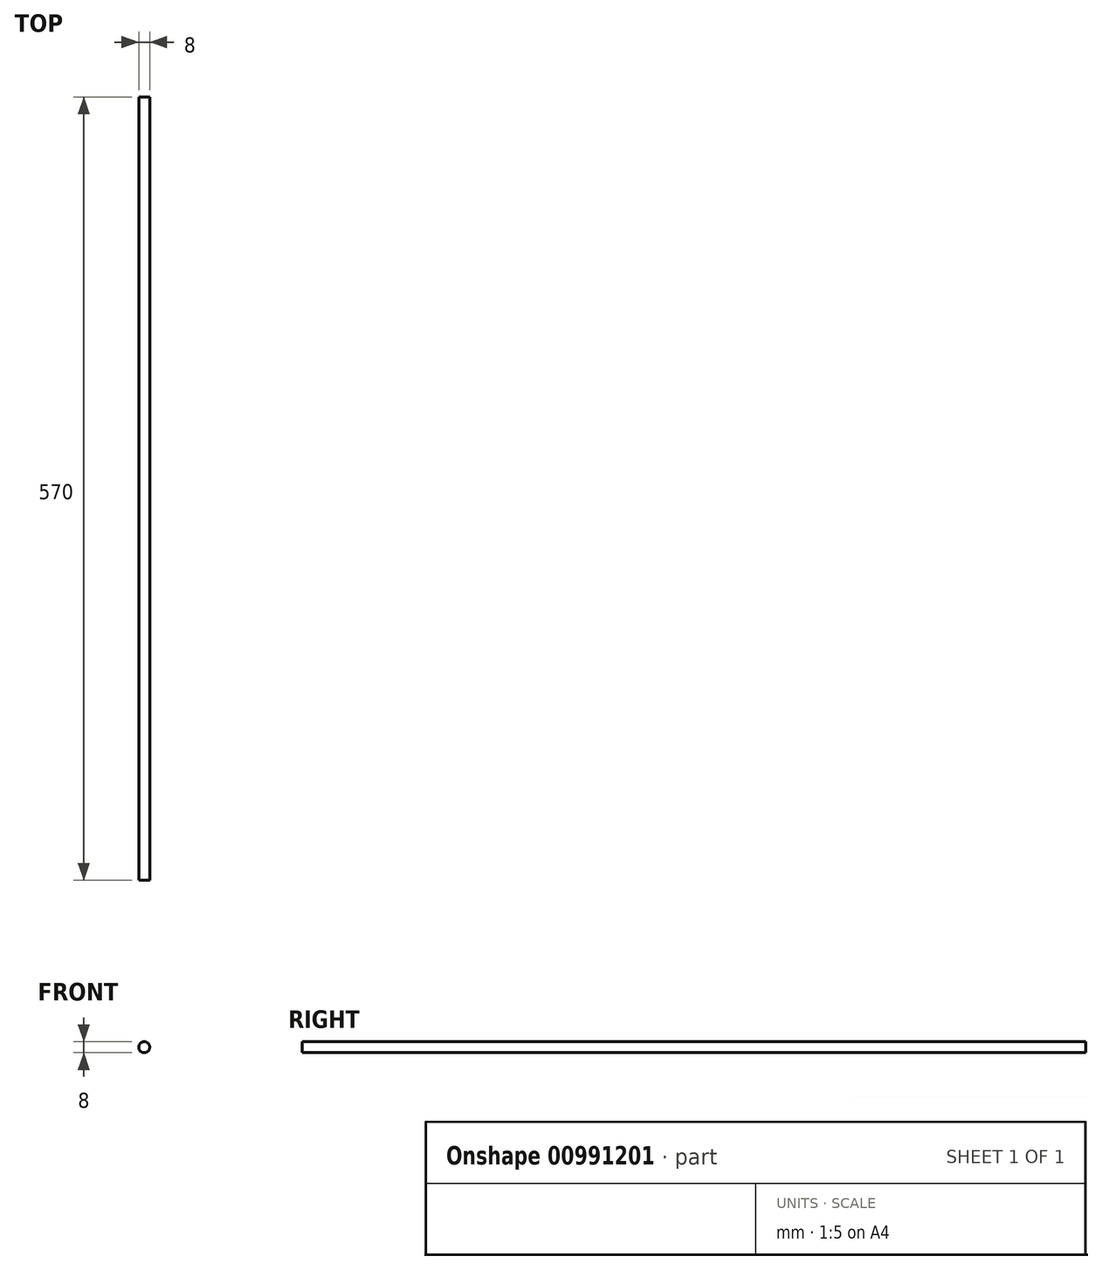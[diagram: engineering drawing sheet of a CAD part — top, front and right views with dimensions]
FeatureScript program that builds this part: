
annotation { "Feature Type Name" : "Feature", "Feature Type Description" : "" }
export const myFeature = defineFeature(function(context is Context, id is Id, definition is map)
    precondition{}
    {
        {
            var Q0;
            Q0=qCreatedBy(makeId("Front.planeOp"),FACE);
            var sketch = newSketch(context, id + "F0", { "sketchPlane" : qUnion([Q0])});
            skCircle(sketch, "E0", {"center": v(0, 0) * mm, "radius": 4 * mm});
            skSolve(sketch);
        }
        {
            var Q0;
            Q0=makeQuery(id+"F0.imprint","IMPRINT",FACE,{"disambiguationData":[TD([[makeQuery(id+"F0.imprint","IMPRINT",EDGE,{"derivedFrom":sQuery(id+"F0.wireOp",EDGE,"E0")}),1.0]])]});
            extrude(context, id + "F1", {"entities" : qUnion([Q0]), "depth" : 570 * mm, "offsetDistance" : 25 * mm, "symmetric" : true});
        }
    });
